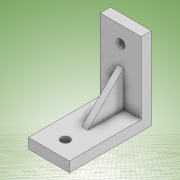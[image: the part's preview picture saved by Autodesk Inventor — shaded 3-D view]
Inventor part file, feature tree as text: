
AUTODESK INVENTOR PART (.ipt)
format: ipt  version: 2022 (Build 260153000, 153)  size: 142,336 bytes
history: native  units: mm
features: sketch x4, extrude x3, other x2, plane x1
ambient origin geometry x8: Origin, YZ Plane, XZ Plane, XY Plane, X Axis, Y Axis, Z Axis, Center Point
bodies: Body1 (feature_tree)
feature tree (10):
  other  "Sólido1"
  extrude  "Extrusión1"  Depth=40.0mm
  extrude  "Extrusión2"  Depth=5.0mm
  plane  "Plano de trabajo1"
  other  "Nervio1"
  extrude  "Extrusión3"  TaperAngle=45.0deg  [1 undecoded]
  sketch  "Boceto1"  dims[d0=20.0mm d1=40.0mm]
  sketch  "Boceto2"  dims[d2=5.0mm d3=0.0mm d4=5.0mm]
  sketch  "Boceto3"  dims[d5=35.0mm d6=0.0mm d7=45.0deg]
  sketch  "Boceto4"  dims[d8=1.0mm d9=3.0mm d10=0.0mm d11=0.0mm d12=1.0mm d13=1.0mm d14=4.3mm d15=8.0mm d16=4.3mm d17=8.0mm d18=5.0mm d19=0.0mm d20=0.5mm d21=0.872665mm d22=0.5mm d23=0.872665mm]
note: 1 required parameter value undecoded (feature->parameter linkage not recoverable at this tier; creation-order binding heuristic only, values carry confidence <= 0.55)
